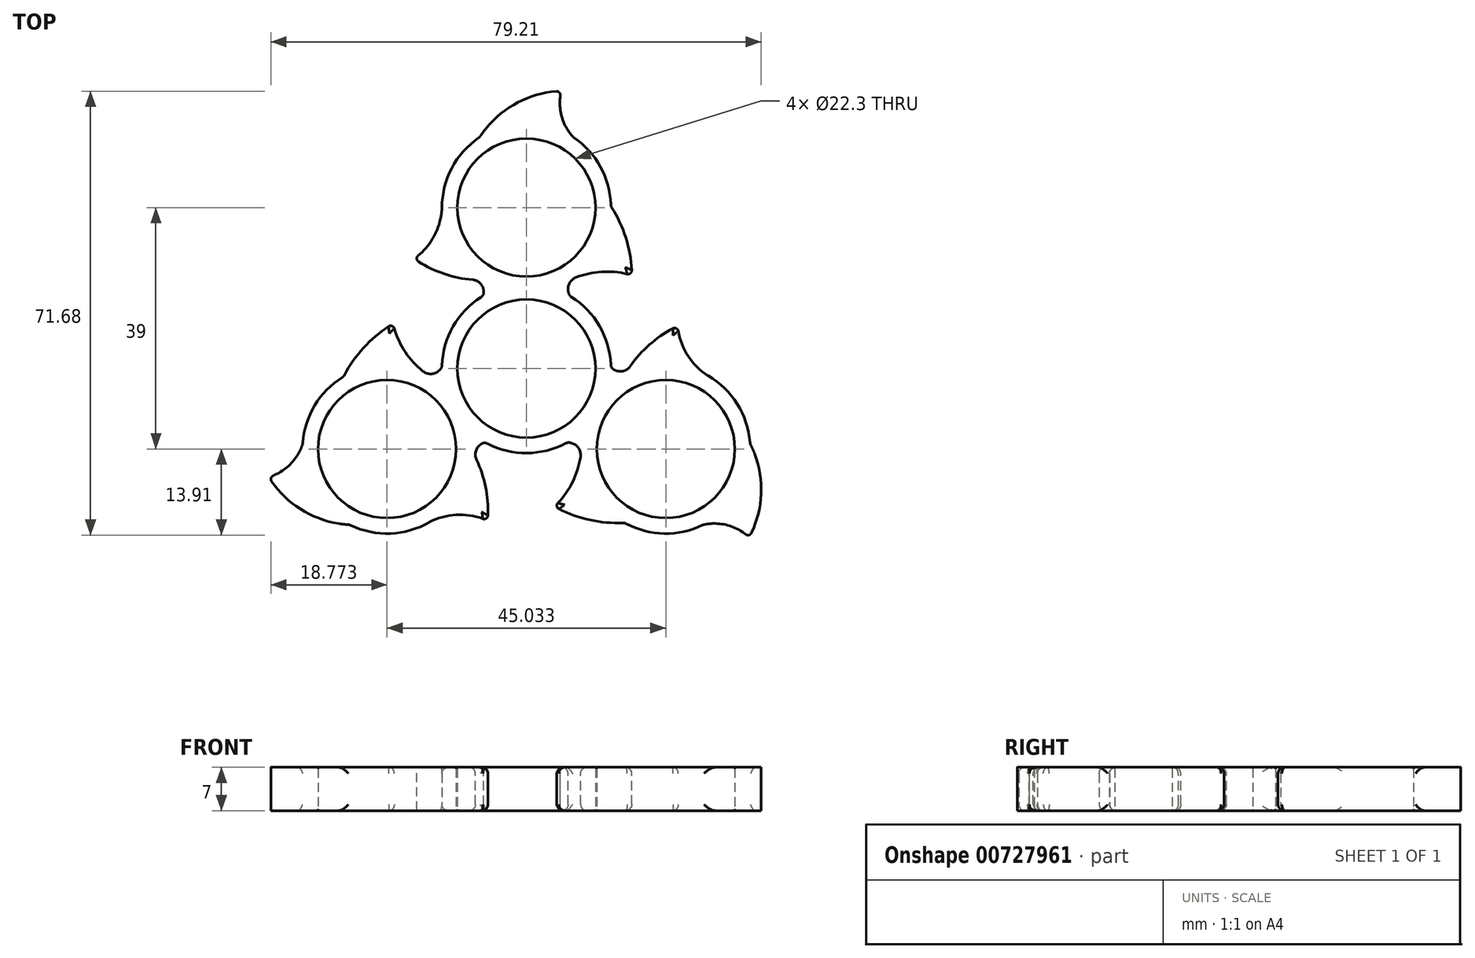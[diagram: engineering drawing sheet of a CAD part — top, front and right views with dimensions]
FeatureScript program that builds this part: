
annotation { "Feature Type Name" : "Feature", "Feature Type Description" : "" }
export const myFeature = defineFeature(function(context is Context, id is Id, definition is map)
    precondition{}
    {
        {
            var Q0;
            Q0=qCreatedBy(makeId("Top.planeOp"),FACE);
            var sketch = newSketch(context, id + "F0", { "sketchPlane" : qUnion([Q0])});
            skCircle(sketch, "E0", {"center": v(0, 0) * mm, "radius": 11.15 * mm});
            skArc(sketch, "E1.0", {"start": v(-5.17, 12.63) * mm, "mid": v(-6.92, 11.76) * mm, "end": v(-8.53, 10.66) * mm, "construction": true});
            skLineSegment(sketch, "E2", {"start": v(0, 0) * mm, "end": v(0, 26) * mm, "construction": true});
            skCircle(sketch, "E3", {"center": v(0, 26) * mm, "radius": 11.15 * mm});
            skArc(sketch, "E4.0", {"start": v(7, 14.28) * mm, "mid": v(0, 39.65) * mm, "end": v(-7, 14.28) * mm});
            skPoint(sketch, "E5.visualSharp", {"position": v(0, 16.7) * mm});
            skLineSegment(sketch, "E6.0", {"start": v(7, 0) * mm, "end": v(7, 29.5) * mm, "construction": true});
            skArc(sketch, "E7.trimOffspring", {"start": v(-7, 11.72) * mm, "mid": v(0, -13.65) * mm, "end": v(7, 11.72) * mm});
            skArc(sketch, "E8", {"start": v(5.6, 44.81) * mm, "mid": v(-1.89, 42.7) * mm, "end": v(-7.56, 37.37) * mm});
            skArc(sketch, "E9", {"start": v(5.6, 44.81) * mm, "mid": v(5.66, 40.85) * mm, "end": v(7.56, 37.37) * mm});
            skArc(sketch, "E10", {"start": v(17.05, 15.05) * mm, "mid": v(16.13, 20.87) * mm, "end": v(13.65, 26.22) * mm});
            skArc(sketch, "E11", {"start": v(17.05, 15.05) * mm, "mid": v(11.95, 15.6) * mm, "end": v(7, 14.28) * mm});
            skArc(sketch, "E12", {"start": v(-18.16, 17.73) * mm, "mid": v(-12.84, 15.15) * mm, "end": v(-7, 14.28) * mm});
            skArc(sketch, "E13", {"start": v(-18.16, 17.73) * mm, "mid": v(-14.96, 21.32) * mm, "end": v(-13.65, 25.94) * mm});
            skArc(sketch, "E14", {"start": v(7, 14.28) * mm, "mid": v(6.7, 13) * mm, "end": v(7, 11.72) * mm});
            skArc(sketch, "E15.MirrorCS", {"start": v(-7, 14.28) * mm, "mid": v(-6.7, 13) * mm, "end": v(-7, 11.72) * mm});
            skSolve(sketch);
        }
        {
            var Q0;
            Q0=qSketchRegion(id+"F2",true);
            var Q1;
            Q1=qSketchRegion(id+"F0",true);
            extrude(context, id + "F1", {"entities" : qUnion([Q0, Q1]), "depth" : 7 * mm, "offsetDistance" : 25 * mm});
        }
        {
            var Q0;
            Q0=qCreatedBy(makeId("Right.planeOp"),FACE);
            var sketch = newSketch(context, id + "F2", { "sketchPlane" : qUnion([Q0])});
            skLineSegment(sketch, "E16", {"start": v(0, -11.35) * mm, "end": v(0, 14.45) * mm, "construction": true});
            skSolve(sketch);
        }
        {
            var Q0;
            Q0=makeQuery(id+"F1.opExtrude","SWEPT_EDGE",EDGE,{"disambiguationData":[OSD([sQuery(id+"F0.wireOp",EDGE,"E4.0"),sQuery(id+"F0.wireOp",EDGE,"E11"),sQuery(id+"F0.wireOp",EDGE,"E14")])]});
            var Q1;
            Q1=makeQuery(id+"F1.opExtrude","SWEPT_EDGE",EDGE,{"disambiguationData":[OSD([sQuery(id+"F0.wireOp",EDGE,"E4.0"),sQuery(id+"F0.wireOp",EDGE,"E12"),sQuery(id+"F0.wireOp",EDGE,"E15.MirrorCS")])]});
            fillet(context, id + "F3", {"entities" : qUnion([Q0, Q1]), "radius" : 2 * mm, "tangentPropagation" : true, "allowEdgeOverflow" : false});
        }
        {
            var Q0;
            Q0=makeQuery(id+"F1.opExtrude","SWEPT_FACE",FACE,{"disambiguationData":[OSD([sQuery(id+"F0.wireOp",EDGE,"E0")])]});
            var Q1;
            Q1=makeQuery(id+"F1.opExtrude","SWEPT_FACE",FACE,{"disambiguationData":[OSD([sQuery(id+"F0.wireOp",EDGE,"E3")])]});
            fillet(context, id + "F4", {"entities" : qUnion([Q0, Q1]), "radius" : 0.2 * mm, "tangentPropagation" : true, "allowEdgeOverflow" : false});
        }
        {
            var Q0;
            Q0=makeQuery(id+"F1.opExtrude","SWEPT_EDGE",EDGE,{"disambiguationData":[OSD([sQuery(id+"F0.wireOp",EDGE,"E8"),sQuery(id+"F0.wireOp",EDGE,"E9")])]});
            var Q1;
            Q1=makeQuery(id+"F1.opExtrude","SWEPT_EDGE",EDGE,{"disambiguationData":[OSD([sQuery(id+"F0.wireOp",EDGE,"E10"),sQuery(id+"F0.wireOp",EDGE,"E11")])]});
            var Q2;
            Q2=makeQuery(id+"F1.opExtrude","SWEPT_EDGE",EDGE,{"disambiguationData":[OSD([sQuery(id+"F0.wireOp",EDGE,"E12"),sQuery(id+"F0.wireOp",EDGE,"E13")])]});
            fillet(context, id + "F5", {"entities" : qUnion([Q0, Q1, Q2]), "radius" : 0.6 * mm, "tangentPropagation" : true, "allowEdgeOverflow" : false});
        }
        {
            var Q0;
            Q0=makeQuery(id+"F1.opExtrude","SWEPT_BODY",BODY,{"disambiguationData":[OSD([sQuery(id+"F0.wireOp",EDGE,"E0"),sQuery(id+"F0.wireOp",EDGE,"E1.0"),sQuery(id+"F0.wireOp",EDGE,"E3"),sQuery(id+"F0.wireOp",EDGE,"E4.0"),sQuery(id+"F0.wireOp",EDGE,"7c884c8c-e37f-41f7-9a8e-9150e4511ce8.0"),sQuery(id+"F0.wireOp",EDGE,"124d70be-8a2f-4ff1-8067-023c3a760d13.0"),sQuery(id+"F0.wireOp",EDGE,"7qioyo7K-iHsX-Xa6s-X97m-BwtuQXfGrCvp"),sQuery(id+"F0.wireOp",EDGE,"oFAU7C9Q-nsB6-dseo-MMuZ-7hNLlDQCrwbt"),sQuery(id+"F0.wireOp",EDGE,"a2486781-22df-47b1-8026-fe576fbc433f.0"),sQuery(id+"F0.wireOp",EDGE,"cb9c9ce2-17e4-408e-8bf5-b38f411324f0.0"),sQuery(id+"F0.wireOp",EDGE,"jKmUo85i-UXFQ-YKQP-mafa-QPdGbBQ2pSZu"),sQuery(id+"F0.wireOp",EDGE,"14rnQz0T-OoW9-SuH9-BmvN-4Fd0IeYT7QfG")])]});
            var Q1;
            Q1=sQuery(id+"F2.wireOp",EDGE,"E16");
            circularPattern(context, id + "F6", {"operationType" : NewBodyOperationType.ADD, "entities" : qUnion([Q0]), "axis" : qUnion([Q1]), "angle" : 360 * degree, "instanceCount" : 3, "equalSpace" : true});
        }
        {
            var Q0;
            {var subQ0=makeQuery(id+"F1.opExtrude","SWEPT_FACE",FACE,{"disambiguationData":[OSD([sQuery(id+"F0.wireOp",EDGE,"E7.trimOffspring")])]});Q0=makeQuery(id+"F6.boolean.opBoolean","MERGE",FACE,{"disambiguationData":[OD(1.0)],"derivedFrom":[subQ0,makeQuery(id+"F6.opPattern","COPY",FACE,{"derivedFrom":subQ0,"instanceName":"1"}),makeQuery(id+"F6.opPattern","COPY",FACE,{"derivedFrom":subQ0,"instanceName":"2"})]});}
            var Q1;
            Q1=makeQuery(id+"F6.opPattern","COPY",FACE,{"derivedFrom":makeQuery(id+"F1.opExtrude","SWEPT_FACE",FACE,{"disambiguationData":[OSD([sQuery(id+"F0.wireOp",EDGE,"E4.0")])]}),"instanceName":"1"});
            var Q2;
            Q2=makeQuery(id+"F6.boolean.opBoolean","SPLIT",FACE,{"derivedFrom":makeQuery(id+"F1.opExtrude","SWEPT_FACE",FACE,{"disambiguationData":[OSD([sQuery(id+"F0.wireOp",EDGE,"E7.trimOffspring")])]})});
            var Q3;
            Q3=makeQuery(id+"F6.opPattern","COPY",FACE,{"derivedFrom":makeQuery(id+"F1.opExtrude","SWEPT_FACE",FACE,{"disambiguationData":[OSD([sQuery(id+"F0.wireOp",EDGE,"30ff2577-5292-4259-b784-18746c50757e2.MirrorCS")])]}),"instanceName":"1"});
            var Q4;
            Q4=makeQuery(id+"F6.opPattern","COPY",FACE,{"derivedFrom":makeQuery(id+"F1.opExtrude","SWEPT_FACE",FACE,{"disambiguationData":[OSD([sQuery(id+"F0.wireOp",EDGE,"69167b42-c78b-48be-9412-8366c6b02a09.filletArc")])]}),"instanceName":"1"});
            var Q5;
            Q5=makeQuery(id+"F6.opPattern","COPY",FACE,{"derivedFrom":makeQuery(id+"F1.opExtrude","SWEPT_FACE",FACE,{"disambiguationData":[OSD([sQuery(id+"F0.wireOp",EDGE,"69167b42-c78b-48be-9412-8366c6b02a09.filletArc")])]}),"instanceName":"2"});
            var Q6;
            Q6=makeQuery(id+"F6.opPattern","COPY",FACE,{"derivedFrom":makeQuery(id+"F1.opExtrude","SWEPT_FACE",FACE,{"disambiguationData":[OSD([sQuery(id+"F0.wireOp",EDGE,"E4.0")])]}),"instanceName":"2"});
            var Q7;
            Q7=makeQuery(id+"F6.opPattern","COPY",FACE,{"derivedFrom":makeQuery(id+"F1.opExtrude","SWEPT_FACE",FACE,{"disambiguationData":[OSD([sQuery(id+"F0.wireOp",EDGE,"30ff2577-5292-4259-b784-18746c50757e2.MirrorCS")])]}),"instanceName":"2"});
            var Q8;
            {var subQ0=makeQuery(id+"F1.opExtrude","SWEPT_FACE",FACE,{"disambiguationData":[OSD([sQuery(id+"F0.wireOp",EDGE,"E7.trimOffspring")])]});Q8=makeQuery(id+"F6.boolean.opBoolean","MERGE",FACE,{"disambiguationData":[OD(0.0)],"derivedFrom":[subQ0,makeQuery(id+"F6.opPattern","COPY",FACE,{"derivedFrom":subQ0,"instanceName":"1"}),makeQuery(id+"F6.opPattern","COPY",FACE,{"derivedFrom":subQ0,"instanceName":"2"})]});}
            var Q9;
            Q9=makeQuery(id+"F1.opExtrude","SWEPT_FACE",FACE,{"disambiguationData":[OSD([sQuery(id+"F0.wireOp",EDGE,"69167b42-c78b-48be-9412-8366c6b02a09.filletArc")])]});
            var Q10;
            Q10=makeQuery(id+"F1.opExtrude","SWEPT_FACE",FACE,{"disambiguationData":[OSD([sQuery(id+"F0.wireOp",EDGE,"E4.0")])]});
            var Q11;
            Q11=makeQuery(id+"F1.opExtrude","SWEPT_FACE",FACE,{"disambiguationData":[OSD([sQuery(id+"F0.wireOp",EDGE,"30ff2577-5292-4259-b784-18746c50757e2.MirrorCS")])]});
            var Q12;
            Q12=makeQuery(id+"F6.opPattern","COPY",EDGE,{"derivedFrom":makeQuery(id+"F1.opExtrude","CAP_EDGE",EDGE,{"disambiguationData":[OSD([sQuery(id+"F0.wireOp",EDGE,"E11")])],"isStart":false}),"instanceName":"2"});
            var Q13;
            Q13=makeQuery(id+"F6.opPattern","COPY",EDGE,{"derivedFrom":makeQuery(id+"F1.opExtrude","CAP_EDGE",EDGE,{"disambiguationData":[OSD([sQuery(id+"F0.wireOp",EDGE,"E11")])],"isStart":true}),"instanceName":"2"});
            var Q14;
            Q14=makeQuery(id+"F6.opPattern","COPY",EDGE,{"derivedFrom":makeQuery(id+"F1.opExtrude","CAP_EDGE",EDGE,{"disambiguationData":[OSD([sQuery(id+"F0.wireOp",EDGE,"SthjhZ3H-fVGO-6kV8-VYfl-ft9CKjtszrES")])],"isStart":true}),"instanceName":"2"});
            var Q15;
            Q15=makeQuery(id+"F6.opPattern","COPY",EDGE,{"derivedFrom":makeQuery(id+"F1.opExtrude","CAP_EDGE",EDGE,{"disambiguationData":[OSD([sQuery(id+"F0.wireOp",EDGE,"SthjhZ3H-fVGO-6kV8-VYfl-ft9CKjtszrES")])],"isStart":false}),"instanceName":"2"});
            var Q16;
            Q16=makeQuery(id+"F1.opExtrude","CAP_EDGE",EDGE,{"disambiguationData":[OSD([sQuery(id+"F0.wireOp",EDGE,"E11")])],"isStart":true});
            var Q17;
            Q17=makeQuery(id+"F1.opExtrude","CAP_EDGE",EDGE,{"disambiguationData":[OSD([sQuery(id+"F0.wireOp",EDGE,"SthjhZ3H-fVGO-6kV8-VYfl-ft9CKjtszrES")])],"isStart":true});
            var Q18;
            Q18=makeQuery(id+"F1.opExtrude","CAP_EDGE",EDGE,{"disambiguationData":[OSD([sQuery(id+"F0.wireOp",EDGE,"E11")])],"isStart":false});
            var Q19;
            Q19=makeQuery(id+"F1.opExtrude","CAP_EDGE",EDGE,{"disambiguationData":[OSD([sQuery(id+"F0.wireOp",EDGE,"SthjhZ3H-fVGO-6kV8-VYfl-ft9CKjtszrES")])],"isStart":false});
            var Q20;
            Q20=makeQuery(id+"F6.opPattern","COPY",EDGE,{"derivedFrom":makeQuery(id+"F1.opExtrude","CAP_EDGE",EDGE,{"disambiguationData":[OSD([sQuery(id+"F0.wireOp",EDGE,"SthjhZ3H-fVGO-6kV8-VYfl-ft9CKjtszrES")])],"isStart":true}),"instanceName":"1"});
            var Q21;
            Q21=makeQuery(id+"F6.opPattern","COPY",EDGE,{"derivedFrom":makeQuery(id+"F1.opExtrude","CAP_EDGE",EDGE,{"disambiguationData":[OSD([sQuery(id+"F0.wireOp",EDGE,"E11")])],"isStart":true}),"instanceName":"1"});
            var Q22;
            Q22=makeQuery(id+"F6.opPattern","COPY",EDGE,{"derivedFrom":makeQuery(id+"F1.opExtrude","CAP_EDGE",EDGE,{"disambiguationData":[OSD([sQuery(id+"F0.wireOp",EDGE,"SthjhZ3H-fVGO-6kV8-VYfl-ft9CKjtszrES")])],"isStart":false}),"instanceName":"1"});
            var Q23;
            Q23=makeQuery(id+"F6.opPattern","COPY",EDGE,{"derivedFrom":makeQuery(id+"F1.opExtrude","CAP_EDGE",EDGE,{"disambiguationData":[OSD([sQuery(id+"F0.wireOp",EDGE,"E11")])],"isStart":false}),"instanceName":"1"});
            var Q24;
            Q24=makeQuery(id+"F6.opPattern","COPY",EDGE,{"derivedFrom":makeQuery(id+"F1.opExtrude","CAP_EDGE",EDGE,{"disambiguationData":[OSD([sQuery(id+"F0.wireOp",EDGE,"E12")])],"isStart":true}),"instanceName":"2"});
            var Q25;
            Q25=makeQuery(id+"F6.opPattern","COPY",EDGE,{"derivedFrom":makeQuery(id+"F1.opExtrude","CAP_EDGE",EDGE,{"disambiguationData":[OSD([sQuery(id+"F0.wireOp",EDGE,"30ff2577-5292-4259-b784-18746c50757e0.MirrorCS")])],"isStart":false}),"instanceName":"2"});
            var Q26;
            Q26=makeQuery(id+"F6.opPattern","COPY",EDGE,{"derivedFrom":makeQuery(id+"F1.opExtrude","CAP_EDGE",EDGE,{"disambiguationData":[OSD([sQuery(id+"F0.wireOp",EDGE,"30ff2577-5292-4259-b784-18746c50757e2.MirrorCS")])],"isStart":false}),"instanceName":"2"});
            var Q27;
            Q27=makeQuery(id+"F6.opPattern","COPY",EDGE,{"derivedFrom":makeQuery(id+"F1.opExtrude","CAP_EDGE",EDGE,{"disambiguationData":[OSD([sQuery(id+"F0.wireOp",EDGE,"E12")])],"isStart":false}),"instanceName":"2"});
            var Q28;
            Q28=makeQuery(id+"F6.opPattern","COPY",EDGE,{"derivedFrom":makeQuery(id+"F1.opExtrude","CAP_EDGE",EDGE,{"disambiguationData":[OSD([sQuery(id+"F0.wireOp",EDGE,"E12")])],"isStart":true}),"instanceName":"1"});
            var Q29;
            Q29=makeQuery(id+"F6.opPattern","COPY",EDGE,{"derivedFrom":makeQuery(id+"F1.opExtrude","CAP_EDGE",EDGE,{"disambiguationData":[OSD([sQuery(id+"F0.wireOp",EDGE,"E13")])],"isStart":true}),"instanceName":"1"});
            var Q30;
            Q30=makeQuery(id+"F6.opPattern","COPY",EDGE,{"derivedFrom":makeQuery(id+"F1.opExtrude","CAP_EDGE",EDGE,{"disambiguationData":[OSD([sQuery(id+"F0.wireOp",EDGE,"30ff2577-5292-4259-b784-18746c50757e0.MirrorCS")])],"isStart":false}),"instanceName":"1"});
            var Q31;
            Q31=makeQuery(id+"F6.opPattern","COPY",EDGE,{"derivedFrom":makeQuery(id+"F1.opExtrude","CAP_EDGE",EDGE,{"disambiguationData":[OSD([sQuery(id+"F0.wireOp",EDGE,"E12")])],"isStart":false}),"instanceName":"1"});
            var Q32;
            Q32=makeQuery(id+"F6.opPattern","COPY",EDGE,{"derivedFrom":makeQuery(id+"F1.opExtrude","CAP_EDGE",EDGE,{"disambiguationData":[OSD([sQuery(id+"F0.wireOp",EDGE,"E13")])],"isStart":false}),"instanceName":"1"});
            var Q33;
            Q33=makeQuery(id+"F6.opPattern","COPY",EDGE,{"derivedFrom":makeQuery(id+"F1.opExtrude","SWEPT_EDGE",EDGE,{"disambiguationData":[OSD([sQuery(id+"F0.wireOp",EDGE,"E12"),sQuery(id+"F0.wireOp",EDGE,"E13")])]}),"instanceName":"1"});
            var Q34;
            Q34=makeQuery(id+"F1.opExtrude","CAP_EDGE",EDGE,{"disambiguationData":[OSD([sQuery(id+"F0.wireOp",EDGE,"30ff2577-5292-4259-b784-18746c50757e2.MirrorCS")])],"isStart":true});
            var Q35;
            Q35=makeQuery(id+"F1.opExtrude","SWEPT_EDGE",EDGE,{"disambiguationData":[OSD([sQuery(id+"F0.wireOp",EDGE,"E4.0"),sQuery(id+"F0.wireOp",EDGE,"30ff2577-5292-4259-b784-18746c50757e0.MirrorCS"),sQuery(id+"F0.wireOp",EDGE,"E12")])]});
            fillet(context, id + "F7", {"entities" : qUnion([Q0, Q1, Q2, Q3, Q4, Q5, Q6, Q7, Q8, Q9, Q10, Q11, Q12, Q13, Q14, Q15, Q16, Q17, Q18, Q19, Q20, Q21, Q22, Q23, Q24, Q25, Q26, Q27, Q28, Q29, Q30, Q31, Q32, Q33, Q34, Q35]), "radius" : 1 * mm, "tangentPropagation" : true, "allowEdgeOverflow" : false});
        }
    });
